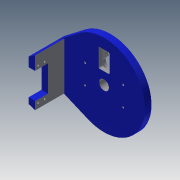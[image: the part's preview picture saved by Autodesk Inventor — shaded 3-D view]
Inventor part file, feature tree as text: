
AUTODESK INVENTOR PART (.ipt)
format: ipt  version: 2013 (Build 170138000, 138)  size: 411,136 bytes
history: native  units: mm
features: sketch x30, extrude x29, fillet x1
ambient origin geometry x8: Origin, YZ Plane, XZ Plane, XY Plane, X Axis, Y Axis, Z Axis, Center Point
bodies: Solid1 (feature_tree)
feature tree (60):
  extrude  "Extrusion1"  Depth=6.0mm
  extrude  "Extrusion2"  Depth=24.3mm
  extrude  "Extrusion3"  Depth=24.3mm
  extrude  "Extrusion4"  Depth=10.0mm
  sketch  "Sketch5"  dims[d9=60.0mm d10=60.0mm]
  extrude  "Extrusion5"  Depth=60.0mm
  extrude  "Extrusion6"  Depth=15.0mm
  extrude  "Extrusion7"  Depth=15.0mm
  extrude  "Extrusion8"  Depth=3.0mm
  extrude  "Extrusion9"  Depth=3.0mm
  extrude  "Extrusion10"  Depth=71.2mm
  extrude  "Extrusion11"  Depth=55.0mm
  extrude  "Extrusion12"  Depth=10.0mm
  extrude  "Extrusion13"  Depth=5.0mm TaperAngle=0.0deg
  extrude  "Extrusion15"  Depth=4.0mm
  extrude  "Extrusion16"  Depth=48.0mm TaperAngle=0.0deg
  extrude  "Extrusion17"  Depth=34.25mm
  extrude  "Extrusion22"  Depth=40.2mm
  sketch  "Sketch24"  dims[d55=49.7mm d56=40.2mm]
  sketch  "Sketch25"  dims[d60=3.0mm d61=3.0mm]
  extrude  "Extrusion23"  Depth=3.0mm
  extrude  "Extrusion24"  Depth=3.0mm
  sketch  "Sketch29"  dims[d64=10.0mm d65=0.0mm d66=3.0mm d67=0.0mm]
  extrude  "Extrusion27"  Depth=3.0mm TaperAngle=0.0deg
  extrude  "Extrusion28"  Depth=4.0mm
  extrude  "Extrusion29"  Depth=8.0mm
  extrude  "Extrusion30"  Depth=15.0mm
  extrude  "Extrusion31"  Depth=6.0mm TaperAngle=0.0deg
  extrude  "Extrusion32"  Depth=14.3mm
  extrude  "Extrusion33"  Depth=48.6mm
  extrude  "Extrusion34"  Depth=35.0mm
  extrude  "Extrusion35"  Depth=35.0mm
  fillet  "Fillet9"  Radius=24.0mm
  extrude  "Extrusion36"  Depth=4.589mm
  sketch  "Sketch1"  dims[d0=120.0mm d1=6.0mm]
  sketch  "Sketch2"  dims[d2=10.0mm d3=0.0mm d4=24.3mm]
  sketch  "Sketch3"  dims[d5=5.0mm d6=24.3mm]
  sketch  "Sketch4"  dims[d7=5.0mm d8=10.0mm]
  sketch  "Sketch6"  dims[d11=15.0mm d12=15.0mm]
  sketch  "Sketch7"  dims[d13=15.0mm d14=15.0mm]
  sketch  "Sketch8"  dims[d15=3.0mm d16=3.0mm]
  sketch  "Sketch9"  dims[d17=3.0mm d18=3.0mm]
  sketch  "Sketch10"  dims[d19=10.0mm d20=0.0mm d31=71.2mm]
  sketch  "Sketch11"  dims[d32=34.25mm d33=55.0mm]
  sketch  "Sketch12"  dims[d34=10.0mm d35=0.0mm d36=10.0mm]
  sketch  "Sketch14"  dims[d37=43.0mm d38=0.0mm d41=5.0mm d42=0.0mm]
  sketch  "Sketch16"  dims[d45=4.0mm d46=4.0mm]
  sketch  "Sketch18"  dims[d47=10.0mm d48=0.0mm d49=48.0mm d50=0.0mm]
  sketch  "Sketch23"  dims[d51=35.0mm d54=34.25mm]
  sketch  "Sketch26"  dims[d62=3.0mm d63=3.0mm]
  sketch  "Sketch30"  dims[d70=14.209mm d71=4.0mm]
  sketch  "Sketch31"  dims[d72=10.0mm d73=0.0mm d74=8.0mm]
  sketch  "Sketch32"  dims[d75=10.0mm d76=0.0mm d78=15.0mm]
  sketch  "Sketch33"  dims[d79=10.0mm d80=6.0mm d81=0.0mm]
  sketch  "Sketch34"  dims[d82=14.3mm d83=14.3mm]
  sketch  "Sketch35"  dims[d84=6.0mm d85=0.0mm d90=48.6mm]
  sketch  "Sketch36"  dims[d91=14.3mm d92=35.0mm]
  sketch  "Sketch37"  dims[d93=14.3mm d94=35.0mm d95=24.0mm d96=0.0mm]
  sketch  "Sketch38"  dims[d97=19.125mm d98=4.589mm]
  sketch  "Sketch39"  dims[d99=10.0mm d100=0.0mm d101=19.125mm d102=4.589mm d103=10.0mm d104=0.0mm d123=15.0mm d124=10.0mm d125=0.0mm d126=35.0mm d129=2.0mm d130=0.0mm d131=10.0mm d132=2.0mm d133=0.0mm d141=63.0mm d142=10.0mm d143=0.0mm d144=7.5mm d145=10.0mm d146=0.0mm d147=3.0mm d148=6.0mm d149=2.0mm d150=10.0mm d151=0.0mm d152=24.0mm d153=0.0mm d154=24.0mm d155=0.0mm d156=6.0mm d157=0.0mm d158=15.0mm d159=24.0mm d160=6.0mm d161=0.0mm d162=16.0mm d163=20.0mm d164=6.0mm d165=0.0mm d166=17.0mm d167=6.0mm d168=0.0mm d169=2.0mm d170=2.0mm d171=0.0mm]
